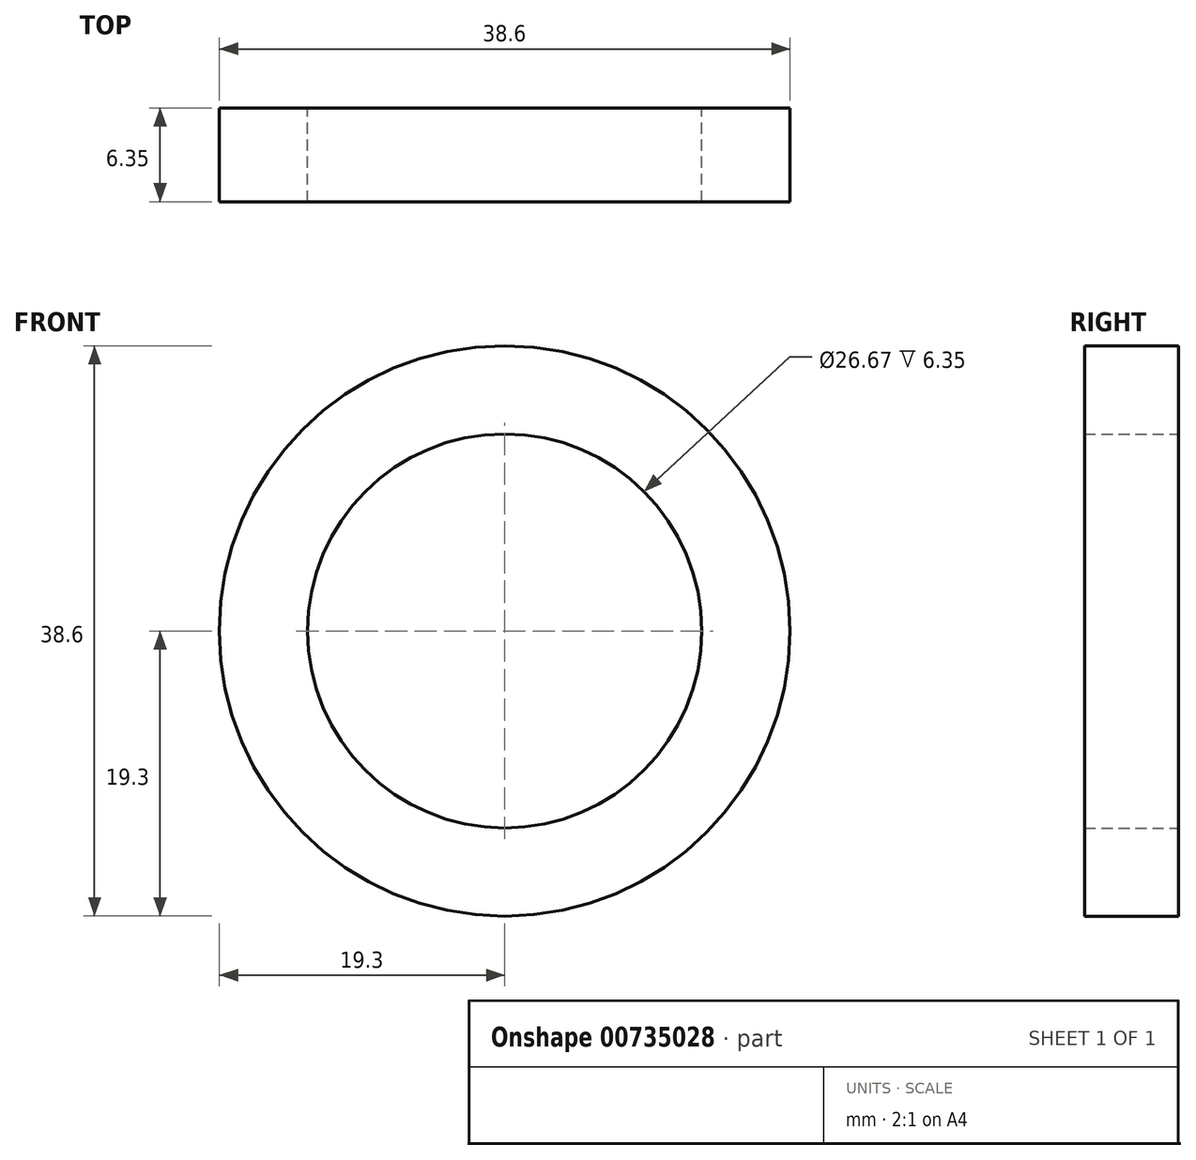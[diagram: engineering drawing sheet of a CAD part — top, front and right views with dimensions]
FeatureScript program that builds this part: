
annotation { "Feature Type Name" : "Feature", "Feature Type Description" : "" }
export const myFeature = defineFeature(function(context is Context, id is Id, definition is map)
    precondition{}
    {
        {
            var Q0;
            Q0=qCreatedBy(makeId("Front.planeOp"),FACE);
            var sketch = newSketch(context, id + "F0", { "sketchPlane" : qUnion([Q0])});
            skCircle(sketch, "E0", {"center": v(0, 0) * mm, "radius": 13.33 * mm});
            skCircle(sketch, "E1", {"center": v(0, 0) * mm, "radius": 19.3 * mm});
            skSolve(sketch);
        }
        {
            var Q0;
            Q0=makeQuery(id+"F0.imprint","IMPRINT",FACE,{"disambiguationData":[TD([[makeQuery(id+"F0.imprint","IMPRINT",EDGE,{"derivedFrom":sQuery(id+"F0.wireOp",EDGE,"E0")}),-1.0]])]});
            extrude(context, id + "F1", {"entities" : qUnion([Q0]), "depth" : 6.35 * mm, "offsetDistance" : 25.4 * mm});
        }
    });
